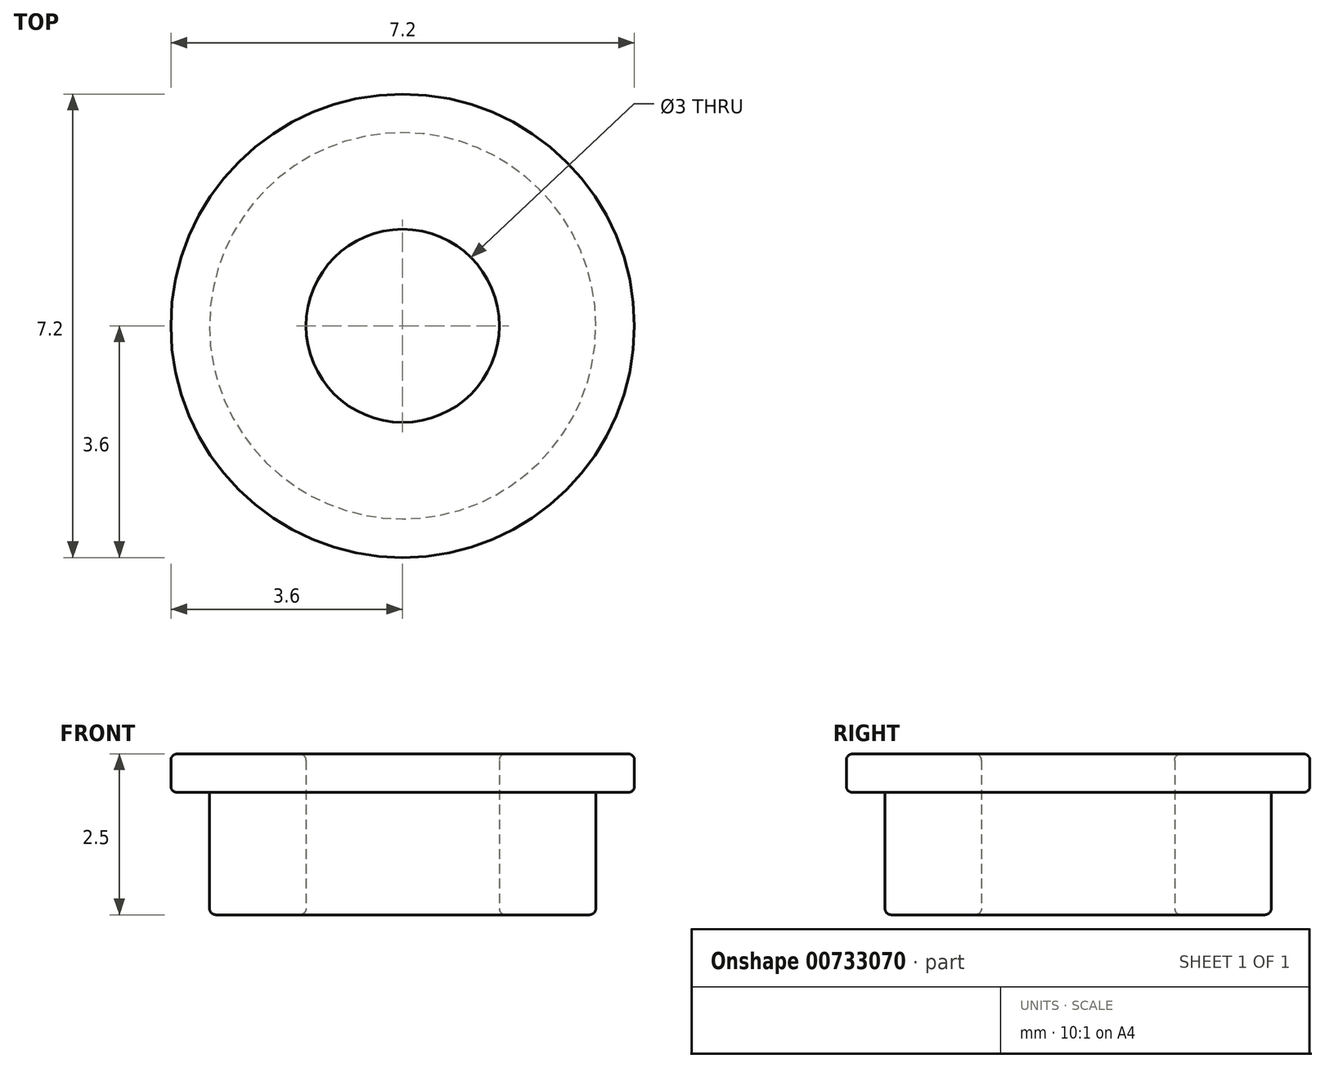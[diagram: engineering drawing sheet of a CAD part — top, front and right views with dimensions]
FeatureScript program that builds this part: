
annotation { "Feature Type Name" : "Feature", "Feature Type Description" : "" }
export const myFeature = defineFeature(function(context is Context, id is Id, definition is map)
    precondition{}
    {
        {
            var Q0;
            Q0=qCreatedBy(makeId("Top.planeOp"),FACE);
            var sketch = newSketch(context, id + "F0", { "sketchPlane" : qUnion([Q0])});
            skCircle(sketch, "E0", {"center": v(0, 0) * mm, "radius": 3 * mm});
            skCircle(sketch, "E1", {"center": v(0, 0) * mm, "radius": 1.5 * mm});
            skCircle(sketch, "E2", {"center": v(0, 0) * mm, "radius": 3.6 * mm});
            skSolve(sketch);
        }
        {
            var Q0;
            Q0=qSketchRegion(id+"F0",true);
            var Q1;
            Q1=makeQuery(id+"F0.imprint","IMPRINT",FACE,{"disambiguationData":[TD([[makeQuery(id+"F0.imprint","IMPRINT",EDGE,{"derivedFrom":sQuery(id+"F0.wireOp",EDGE,"E0")}),1.0]])]});
            extrude(context, id + "F1", {"entities" : qUnion([Q0, Q1]), "depth" : 0.6 * mm, "offsetDistance" : 25 * mm});
        }
        {
            var Q0;
            Q0=makeQuery(id+"F0.imprint","IMPRINT",FACE,{"disambiguationData":[TD([[makeQuery(id+"F0.imprint","IMPRINT",EDGE,{"derivedFrom":sQuery(id+"F0.wireOp",EDGE,"E0")}),1.0]])]});
            extrude(context, id + "F2", {"entities" : qUnion([Q0]), "operationType" : NewBodyOperationType.ADD, "oppositeDirection" : true, "depth" : (2.5 - 0.6) * mm, "offsetDistance" : 25 * mm});
        }
        {
            var Q0;
            Q0=makeQuery(id+"F2.opExtrude","CAP_EDGE",EDGE,{"disambiguationData":[OSD([sQuery(id+"F0.wireOp",EDGE,"E0")])],"isStart":false});
            var Q1;
            Q1=makeQuery(id+"F2.opExtrude","CAP_EDGE",EDGE,{"disambiguationData":[OSD([sQuery(id+"F0.wireOp",EDGE,"E1")])],"isStart":false});
            var Q2;
            Q2=makeQuery(id+"F2.opExtrude","CAP_EDGE",EDGE,{"disambiguationData":[OSD([sQuery(id+"F0.wireOp",EDGE,"E0")])],"isStart":true});
            var Q3;
            Q3=makeQuery(id+"F1.opExtrude","CAP_EDGE",EDGE,{"disambiguationData":[OSD([sQuery(id+"F0.wireOp",EDGE,"E2")])],"isStart":true});
            var Q4;
            Q4=makeQuery(id+"F1.opExtrude","CAP_EDGE",EDGE,{"disambiguationData":[OSD([sQuery(id+"F0.wireOp",EDGE,"E2")])],"isStart":false});
            var Q5;
            Q5=makeQuery(id+"F1.opExtrude","CAP_EDGE",EDGE,{"disambiguationData":[OSD([sQuery(id+"F0.wireOp",EDGE,"E1")])],"isStart":false});
            fillet(context, id + "F3", {"entities" : qUnion([Q0, Q1, Q2, Q3, Q4, Q5]), "radius" : 0.1 * mm, "tangentPropagation" : true, "allowEdgeOverflow" : false});
        }
    });
